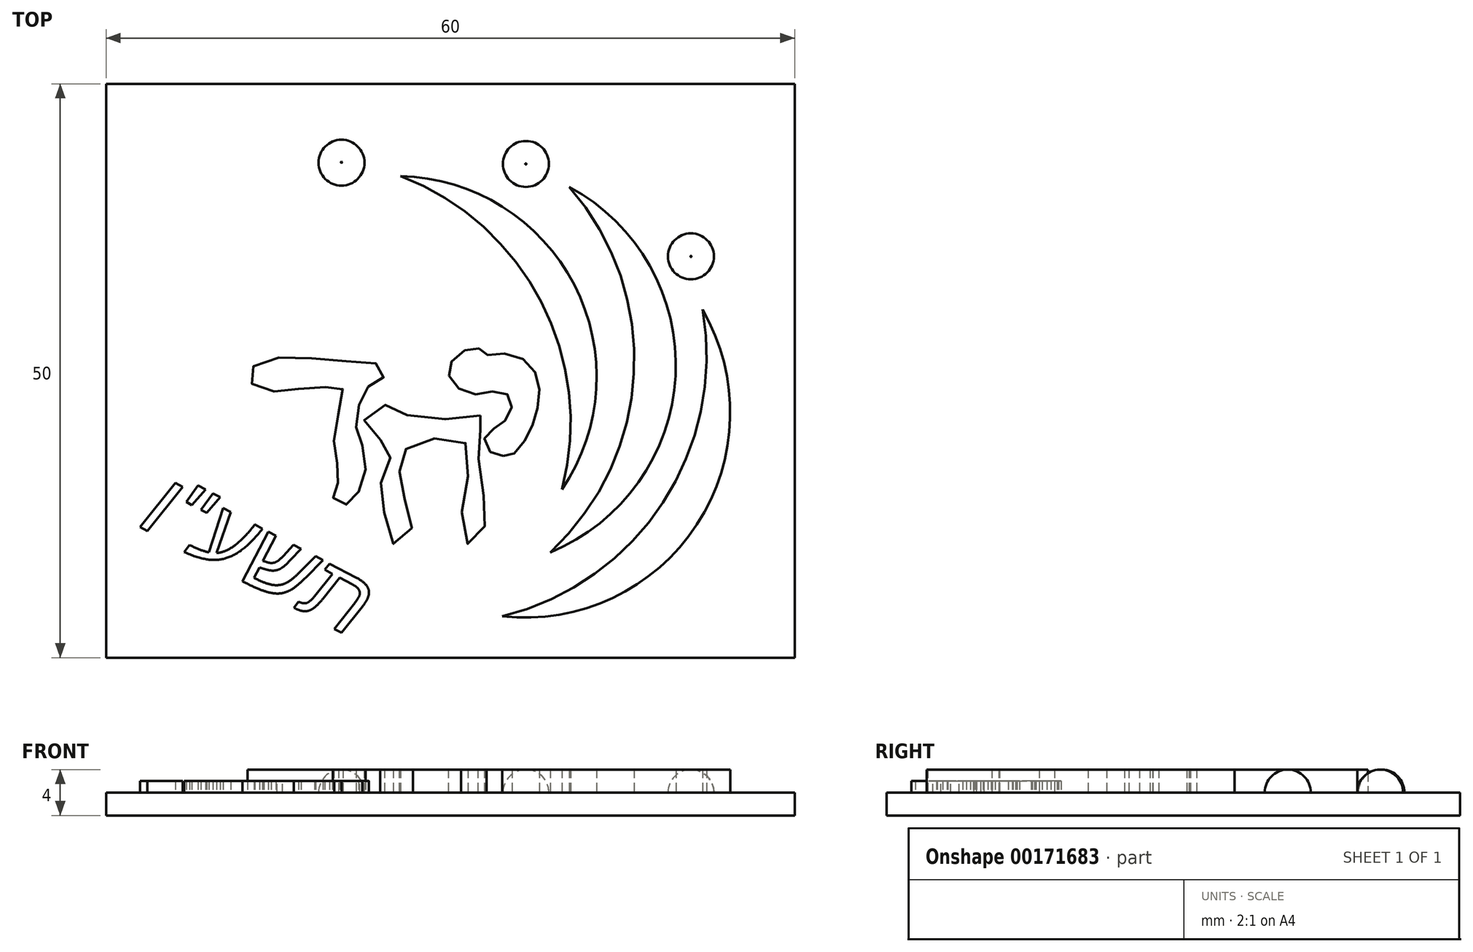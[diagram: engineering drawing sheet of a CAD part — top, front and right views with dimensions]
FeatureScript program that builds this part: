
annotation { "Feature Type Name" : "Feature", "Feature Type Description" : "" }
export const myFeature = defineFeature(function(context is Context, id is Id, definition is map)
    precondition{}
    {
        {
            var Q0;
            Q0=qCreatedBy(makeId("Top.planeOp"),FACE);
            var sketch = newSketch(context, id + "F0", { "sketchPlane" : qUnion([Q0])});
            skLineSegment(sketch, "E0.bottom", {"start": v(30, -25) * mm, "end": v(-30, -25) * mm});
            skLineSegment(sketch, "E0.top", {"start": v(30, 25) * mm, "end": v(-30, 25) * mm});
            skLineSegment(sketch, "E0.left", {"start": v(30, -25) * mm, "end": v(30, 25) * mm});
            skLineSegment(sketch, "E0.right", {"start": v(-30, -25) * mm, "end": v(-30, 25) * mm});
            skPoint(sketch, "E0.middle", {"position": v(0, 0) * mm});
            skSolve(sketch);
        }
        {
            var Q0;
            Q0 = qSketchRegion(id + "F0", true);
            extrude(context, id + "F1", {"entities" : qUnion([Q0]), "depth" : 2 * mm});
        }
        {
            var Q0;
            Q0=makeQuery(id+"F1.opExtrude","CAP_FACE",FACE,{"disambiguationData":[OSD([sQuery(id+"F0.wireOp",EDGE,"E0.bottom"),sQuery(id+"F0.wireOp",EDGE,"E0.top"),sQuery(id+"F0.wireOp",EDGE,"E0.left"),sQuery(id+"F0.wireOp",EDGE,"E0.right")])],"isStart":false});
            var sketch = newSketch(context, id + "F2", { "sketchPlane" : qUnion([Q0])});
            skArc(sketch, "E1", {"start": v(4.53, -21.4) * mm, "mid": v(18.52, -11.48) * mm, "end": v(21.96, 5.33) * mm});
            skArc(sketch, "E2", {"start": v(4.53, -21.4) * mm, "mid": v(21.48, -13.4) * mm, "end": v(21.96, 5.33) * mm});
            skArc(sketch, "E3", {"start": v(8.7, -15.82) * mm, "mid": v(15.99, -0.24) * mm, "end": v(10.37, 16.02) * mm});
            skArc(sketch, "E4", {"start": v(8.7, -15.82) * mm, "mid": v(19.62, -0.43) * mm, "end": v(10.37, 16.02) * mm});
            skArc(sketch, "E5", {"start": v(9.73, -10.34) * mm, "mid": v(7.91, 6) * mm, "end": v(-4.35, 16.97) * mm});
            skArc(sketch, "E6", {"start": v(9.73, -10.34) * mm, "mid": v(10.8, 7.49) * mm, "end": v(-4.35, 16.97) * mm});
            skCircle(sketch, "E7", {"center": v(20.96, 9.97) * mm, "radius": 0.05 * mm});
            skCircle(sketch, "E8", {"center": v(6.58, 18.02) * mm, "radius": 0.05 * mm});
            skCircle(sketch, "E9", {"center": v(-9.49, 18.17) * mm, "radius": 0.05 * mm});
            skFitSpline(sketch, "E10", {"points": [v(4.6, -7.43) * mm, v(5.48, -7.27) * mm, v(6.57, -5.94) * mm, v(7.44, -3.9) * mm, v(7.74, -1.57) * mm, v(7.05, 0.38) * mm, v(4.95, 1.48) * mm, v(3.07, 1.43) * mm, v(2.46, 1.95) * mm, v(1.02, 1.64) * mm, v(-0.17, 0.23) * mm, v(0.35, -1.22) * mm, v(2.23, -2.05) * mm, v(4.12, -1.79) * mm, v(5.31, -2.48) * mm, v(5.02, -3.97) * mm, v(4.16, -4.86) * mm, v(3.03, -5.7) * mm, v(3.4, -7.01) * mm, v(4.6, -7.43) * mm]});
            skFitSpline(sketch, "E11", {"points": [v(2.6, -3.9) * mm, v(0.24, -4.25) * mm, v(-2.36, -3.9) * mm, v(-4.83, -3.7) * mm, v(-5.42, -3.04) * mm, v(-6.87, -3.31) * mm, v(-7.5, -4.46) * mm, v(-6.78, -5.7) * mm, v(-5.57, -6.29) * mm, v(-5, -7.16) * mm, v(-5.92, -8.4) * mm, v(-6.07, -9.8) * mm, v(-5.86, -11.68) * mm, v(-5.65, -13.09) * mm, v(-4.9, -15.13) * mm, v(-3.95, -14.48) * mm, v(-3.27, -13.34) * mm, v(-3.9, -11.41) * mm, v(-4.3, -9.85) * mm, v(-4.45, -8.6) * mm, v(-4.38, -7.82) * mm, v(-3.56, -6.45) * mm, v(-2.1, -5.96) * mm, v(1.14, -5.96) * mm, v(1.31, -6.54) * mm, v(1.53, -8.82) * mm, v(1.11, -11.58) * mm, v(0.96, -13.56) * mm, v(1.7, -15.19) * mm, v(2.69, -14.23) * mm, v(3.15, -12.7) * mm, v(2.85, -10.64) * mm, v(2.47, -7.93) * mm, v(2.43, -5.9) * mm, v(2.77, -4.91) * mm, v(3.15, -4.3) * mm, v(2.6, -3.9) * mm]});
            skFitSpline(sketch, "E12", {"points": [v(-9.82, -9.77) * mm, v(-10.24, -10.73) * mm, v(-9.87, -11.56) * mm, v(-8.83, -11.56) * mm, v(-7.99, -10.56) * mm, v(-7.38, -8.44) * mm, v(-7.78, -6.25) * mm, v(-8.22, -4.88) * mm, v(-7.95, -2.94) * mm, v(-7.2, -1.43) * mm, v(-5.99, -0.84) * mm, v(-5.9, 0.32) * mm, v(-8.22, 0.78) * mm, v(-12.85, 1.14) * mm, v(-16.48, 0.8) * mm, v(-17.66, -0.54) * mm, v(-16.18, -1.74) * mm, v(-13.97, -1.62) * mm, v(-11.15, -1.45) * mm, v(-9.47, -1.41) * mm, v(-9.7, -3.5) * mm, v(-10.16, -6.35) * mm, v(-9.84, -8.25) * mm, v(-9.82, -9.77) * mm]});
            skSolve(sketch);
        }
        {
            var Q0;
            Q0 = qSketchRegion(id + "F2", true);
            extrude(context, id + "F3", {"entities" : qUnion([Q0]), "operationType" : NewBodyOperationType.ADD, "depth" : 2 * mm});
        }
        {
            var Q0;
            Q0=makeQuery(id+"F1.opExtrude","CAP_FACE",FACE,{"disambiguationData":[OSD([sQuery(id+"F0.wireOp",EDGE,"E0.bottom"),sQuery(id+"F0.wireOp",EDGE,"E0.top"),sQuery(id+"F0.wireOp",EDGE,"E0.left"),sQuery(id+"F0.wireOp",EDGE,"E0.right")])],"isStart":false});
            var sketch = newSketch(context, id + "F4", { "sketchPlane" : qUnion([Q0])});
            skText(sketch, "E13", { "text": "ו\"עשת", "fontName": "Arimo-Italic.ttf"});
            const initialGuessF4  = {"E13": [-0.0273, -0.0135, 0.88594, -0.4638, 0.00582]};
            skSetInitialGuess(sketch, initialGuessF4);
            skSolve(sketch);
        }
        {
            var Q0;
            Q0 = qSketchRegion(id + "F4", true);
            extrude(context, id + "F5", {"entities" : qUnion([Q0]), "operationType" : NewBodyOperationType.ADD, "depth" : 1 * mm});
        }
        {
            var Q0;
            Q0=makeQuery(id+"F3.opExtrude","SWEPT_FACE",FACE,{"disambiguationData":[OSD([sQuery(id+"F2.wireOp",EDGE,"E9")])]});
            cPlane(context, id + "F6", {"entities" : qUnion([Q0]), "cplaneType" : CPlaneType.LINE_ANGLE, "offset" : 25 * mm, "angle" : 0 * degree, "width" : 150 * mm, "height" : 150 * mm});
        }
        {
            var Q0;
            Q0=makeQuery(id+"F3.opExtrude","SWEPT_FACE",FACE,{"disambiguationData":[OSD([sQuery(id+"F2.wireOp",EDGE,"E8")])]});
            cPlane(context, id + "F7", {"entities" : qUnion([Q0]), "cplaneType" : CPlaneType.LINE_ANGLE, "offset" : 25 * mm, "angle" : 0 * degree, "width" : 150 * mm, "height" : 150 * mm});
        }
        {
            var Q0;
            Q0=makeQuery(id+"F3.opExtrude","SWEPT_FACE",FACE,{"disambiguationData":[OSD([sQuery(id+"F2.wireOp",EDGE,"E7")])]});
            cPlane(context, id + "F8", {"entities" : qUnion([Q0]), "cplaneType" : CPlaneType.LINE_ANGLE, "offset" : 25 * mm, "angle" : 0 * degree, "width" : 150 * mm, "height" : 150 * mm});
        }
        {
            var Q0;
            Q0=qCreatedBy(id+"F6.planeOp",FACE);
            var sketch = newSketch(context, id + "F9", { "sketchPlane" : qUnion([Q0])});
            skLineSegment(sketch, "E14", {"start": v(-18.13, 4) * mm, "end": v(-18.13, 2) * mm});
            skLineSegment(sketch, "E15", {"start": v(-18.13, 2) * mm, "end": v(-20.13, 2) * mm});
            skArc(sketch, "E16", {"start": v(-18.13, 4) * mm, "mid": v(-19.54, 3.41) * mm, "end": v(-20.13, 2) * mm});
            skSolve(sketch);
        }
        {
            var Q0;
            Q0 = qSketchRegion(id + "F9", true);
            var Q1;
            Q1=sQuery(id+"F9.wireOp",EDGE,"E14");
            revolve(context, id + "F10", {"operationType" : NewBodyOperationType.ADD, "entities" : qUnion([Q0]), "axis" : qUnion([Q1]), "revolveType" : RevolveType.FULL});
        }
        {
            var Q0;
            Q0=qCreatedBy(id+"F7.planeOp",FACE);
            var sketch = newSketch(context, id + "F11", { "sketchPlane" : qUnion([Q0])});
            skLineSegment(sketch, "E17", {"start": v(-18.02, 4) * mm, "end": v(-18.02, 2) * mm});
            skLineSegment(sketch, "E18", {"start": v(-18.02, 2) * mm, "end": v(-20.02, 2) * mm});
            skArc(sketch, "E19", {"start": v(-18.02, 4) * mm, "mid": v(-19.44, 3.41) * mm, "end": v(-20.02, 2) * mm});
            skSolve(sketch);
        }
        {
            var Q0;
            Q0 = qSketchRegion(id + "F11", true);
            var Q1;
            Q1=sQuery(id+"F11.wireOp",EDGE,"E17");
            revolve(context, id + "F12", {"operationType" : NewBodyOperationType.ADD, "entities" : qUnion([Q0]), "axis" : qUnion([Q1]), "revolveType" : RevolveType.FULL});
        }
        {
            var Q0;
            Q0=qCreatedBy(id+"F8.planeOp",FACE);
            var sketch = newSketch(context, id + "F13", { "sketchPlane" : qUnion([Q0])});
            skLineSegment(sketch, "E20", {"start": v(-11.97, 2) * mm, "end": v(-9.97, 2) * mm});
            skLineSegment(sketch, "E21", {"start": v(-9.97, 2) * mm, "end": v(-9.97, 4) * mm});
            skArc(sketch, "E22", {"start": v(-9.97, 4) * mm, "mid": v(-11.38, 3.41) * mm, "end": v(-11.97, 2) * mm});
            skSolve(sketch);
        }
        {
            var Q0;
            Q0 = qSketchRegion(id + "F13", true);
            var Q1;
            Q1=sQuery(id+"F13.wireOp",EDGE,"E21");
            revolve(context, id + "F14", {"operationType" : NewBodyOperationType.ADD, "entities" : qUnion([Q0]), "axis" : qUnion([Q1]), "revolveType" : RevolveType.FULL});
        }
    });
